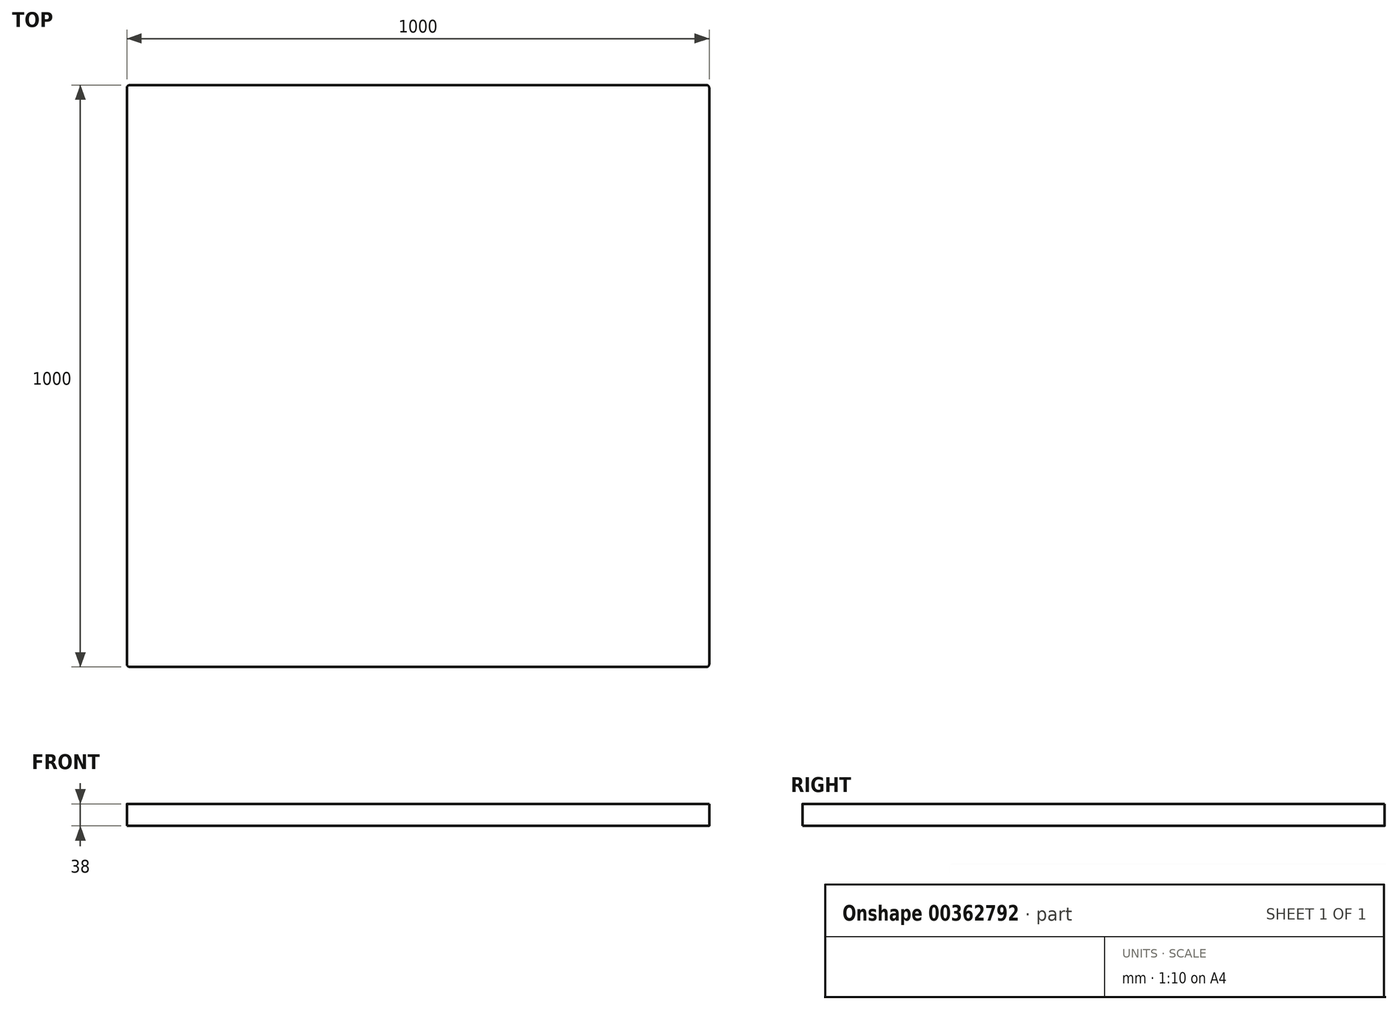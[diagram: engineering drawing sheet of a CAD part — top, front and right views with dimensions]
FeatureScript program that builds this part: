
annotation { "Feature Type Name" : "Feature", "Feature Type Description" : "" }
export const myFeature = defineFeature(function(context is Context, id is Id, definition is map)
    precondition{}
    {
        {
            var Q0;
            Q0=qCreatedBy(makeId("Top.planeOp"),FACE);
            var sketch = newSketch(context, id + "F0", { "sketchPlane" : qUnion([Q0])});
            skLineSegment(sketch, "E0.bottom", {"start": v(500, 500) * mm, "end": v(-500, 500) * mm});
            skLineSegment(sketch, "E0.top", {"start": v(500, -500) * mm, "end": v(-500, -500) * mm});
            skLineSegment(sketch, "E0.left", {"start": v(500, 500) * mm, "end": v(500, -500) * mm});
            skLineSegment(sketch, "E0.right", {"start": v(-500, 500) * mm, "end": v(-500, -500) * mm});
            skPoint(sketch, "E0.middle", {"position": v(0, 0) * mm});
            skSolve(sketch);
        }
        {
            var Q0;
            Q0=makeQuery(id+"F0.imprint","IMPRINT",FACE,{"disambiguationData":[TD([[makeQuery(id+"F0.imprint","IMPRINT",EDGE,{"derivedFrom":sQuery(id+"F0.wireOp",EDGE,"E0.bottom")}),1.0]])]});
            extrude(context, id + "F1", {"entities" : qUnion([Q0]), "depth" : 38 * mm});
        }
        {
            var Q0;
            Q0=makeQuery(id+"F1.opExtrude","SWEPT_EDGE",EDGE,{"disambiguationData":[OSD([sQuery(id+"F0.wireOp",EDGE,"E0.top"),sQuery(id+"F0.wireOp",EDGE,"E0.right")])]});
            var Q1;
            Q1=makeQuery(id+"F1.opExtrude","SWEPT_EDGE",EDGE,{"disambiguationData":[OSD([sQuery(id+"F0.wireOp",EDGE,"E0.bottom"),sQuery(id+"F0.wireOp",EDGE,"E0.right")])]});
            var Q2;
            Q2=makeQuery(id+"F1.opExtrude","SWEPT_EDGE",EDGE,{"disambiguationData":[OSD([sQuery(id+"F0.wireOp",EDGE,"E0.bottom"),sQuery(id+"F0.wireOp",EDGE,"E0.left")])]});
            var Q3;
            Q3=makeQuery(id+"F1.opExtrude","SWEPT_EDGE",EDGE,{"disambiguationData":[OSD([sQuery(id+"F0.wireOp",EDGE,"E0.top"),sQuery(id+"F0.wireOp",EDGE,"E0.left")])]});
            fillet(context, id + "F2", {"entities" : qUnion([Q0, Q1, Q2, Q3]), "radius" : 5 * mm, "tangentPropagation" : true, "allowEdgeOverflow" : false});
        }
    });
